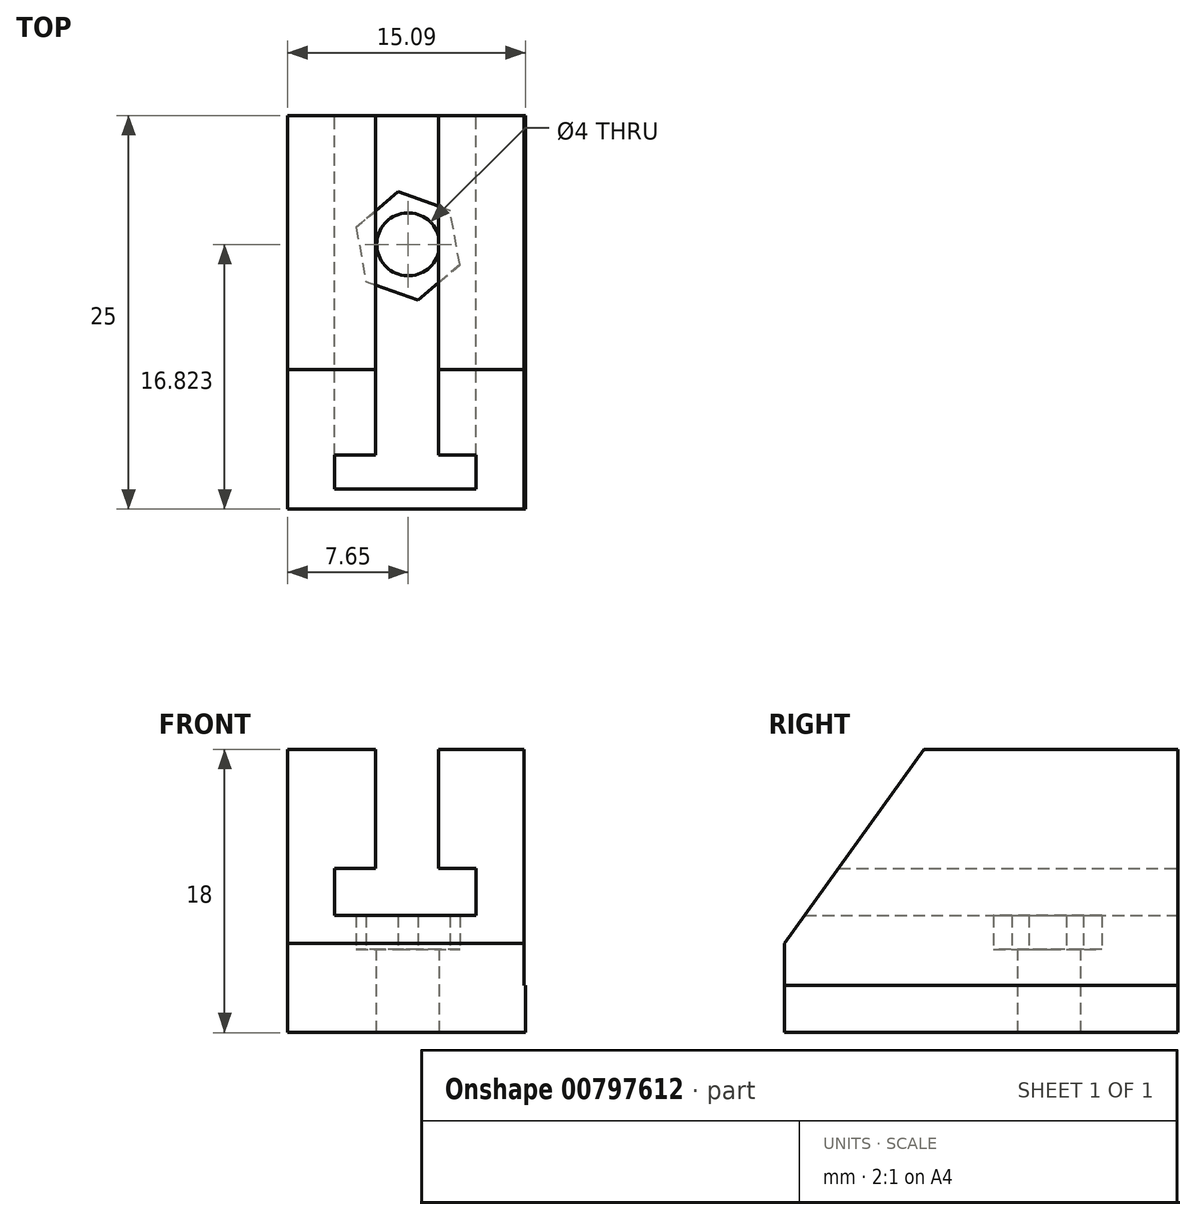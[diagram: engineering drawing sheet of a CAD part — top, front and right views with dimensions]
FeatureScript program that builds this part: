
annotation { "Feature Type Name" : "Feature", "Feature Type Description" : "" }
export const myFeature = defineFeature(function(context is Context, id is Id, definition is map)
    precondition{}
    {
        {
            var Q0;
            Q0=qCreatedBy(makeId("Front.planeOp"),FACE);
            var sketch = newSketch(context, id + "F0", { "sketchPlane" : qUnion([Q0])});
            skLineSegment(sketch, "E0.bottom", {"start": v(-7.65, 12.72) * mm, "end": v(-2.07, 12.72) * mm});
            skLineSegment(sketch, "E0.top", {"start": v(-7.65, -2.28) * mm, "end": v(7.35, -2.28) * mm});
            skLineSegment(sketch, "E0.left", {"start": v(-7.65, 12.72) * mm, "end": v(-7.65, -2.28) * mm});
            skLineSegment(sketch, "E0.right", {"start": v(7.35, 12.72) * mm, "end": v(7.35, -2.28) * mm});
            skLineSegment(sketch, "E1.bottom", {"start": v(-4.69, 5.16) * mm, "end": v(-2.07, 5.16) * mm});
            skLineSegment(sketch, "E1.top", {"start": v(-4.69, 2.16) * mm, "end": v(4.31, 2.16) * mm});
            skLineSegment(sketch, "E1.left", {"start": v(-4.69, 5.16) * mm, "end": v(-4.69, 2.16) * mm});
            skLineSegment(sketch, "E1.right", {"start": v(4.31, 5.16) * mm, "end": v(4.31, 2.16) * mm});
            skLineSegment(sketch, "E2.left", {"start": v(-2.07, 5.16) * mm, "end": v(-2.07, 12.72) * mm});
            skLineSegment(sketch, "E2.right", {"start": v(1.93, 5.16) * mm, "end": v(1.93, 12.72) * mm});
            skLineSegment(sketch, "E3.trimOffspring", {"start": v(1.93, 5.16) * mm, "end": v(4.31, 5.16) * mm});
            skLineSegment(sketch, "E4.bottom", {"start": v(-7.65, -2.28) * mm, "end": v(7.44, -2.28) * mm});
            skLineSegment(sketch, "E4.top", {"start": v(-7.65, -5.28) * mm, "end": v(7.44, -5.28) * mm});
            skLineSegment(sketch, "E4.left", {"start": v(-7.65, -2.28) * mm, "end": v(-7.65, -5.28) * mm});
            skLineSegment(sketch, "E4.right", {"start": v(7.44, -2.28) * mm, "end": v(7.44, -5.28) * mm});
            skLineSegment(sketch, "E5.trimOffspring", {"start": v(1.93, 12.72) * mm, "end": v(7.35, 12.72) * mm});
            skSolve(sketch);
        }
        {
            var Q0;
            Q0=makeQuery(id+"F0.imprint","IMPRINT",FACE,{"disambiguationData":[TD([[makeQuery(id+"F0.imprint","IMPRINT",EDGE,{"derivedFrom":sQuery(id+"F0.wireOp",EDGE,"E0.bottom")}),-1.0]])]});
            var Q1;
            Q1=makeQuery(id+"F0.imprint","IMPRINT",FACE,{"disambiguationData":[TD([[makeQuery(id+"F0.imprint","IMPRINT",EDGE,{"derivedFrom":sQuery(id+"F0.wireOp",EDGE,"E4.top")}),1.0]])]});
            extrude(context, id + "F1", {"entities" : qUnion([Q0, Q1]), "depth" : 25 * mm, "offsetDistance" : 25 * mm});
        }
        {
            var Q0;
            Q0=qCreatedBy(makeId("Right.planeOp"),FACE);
            var sketch = newSketch(context, id + "F2", { "sketchPlane" : qUnion([Q0])});
            skLineSegment(sketch, "E6", {"start": v(-27.17, -2.65) * mm, "end": v(-14.12, 15.54) * mm});
            skLineSegment(sketch, "E7", {"start": v(-14.12, 15.54) * mm, "end": v(-30.08, 15.54) * mm});
            skLineSegment(sketch, "E8", {"start": v(-30.08, 15.54) * mm, "end": v(-27.17, -2.65) * mm});
            skSolve(sketch);
        }
        {
            var Q0;
            Q0=makeQuery(id+"F2.imprint","IMPRINT",FACE,{"disambiguationData":[TD([[makeQuery(id+"F2.imprint","IMPRINT",EDGE,{"derivedFrom":sQuery(id+"F2.wireOp",EDGE,"E6")}),1.0]])]});
            extrude(context, id + "F3", {"entities" : qUnion([Q0]), "operationType" : NewBodyOperationType.REMOVE, "endBound" : BoundingType.SYMMETRIC, "oppositeDirection" : true, "depth" : 37.4 * mm, "offsetDistance" : 25 * mm});
        }
        {
            var Q0;
            Q0=qCreatedBy(makeId("Top.planeOp"),FACE);
            var sketch = newSketch(context, id + "F4", { "sketchPlane" : qUnion([Q0])});
            skPoint(sketch, "E9.0.midPoint", {"position": v(2.48, -5.83) * mm});
            skLineSegment(sketch, "E10.0", {"start": v(2.65, -6.02) * mm, "end": v(3.28, -9.46) * mm});
            skLineSegment(sketch, "E10.1", {"start": v(3.28, -9.46) * mm, "end": v(0.6, -11.73) * mm});
            skLineSegment(sketch, "E10.2", {"start": v(0.6, -11.73) * mm, "end": v(-2.69, -10.55) * mm});
            skLineSegment(sketch, "E10.3", {"start": v(-2.69, -10.55) * mm, "end": v(-3.31, -7.1) * mm});
            skLineSegment(sketch, "E10.4", {"start": v(-3.31, -7.1) * mm, "end": v(-0.64, -4.84) * mm});
            skLineSegment(sketch, "E10.5", {"start": v(-0.64, -4.84) * mm, "end": v(2.65, -6.02) * mm});
            skPoint(sketch, "E11.orphan", {"position": v(-3.1, -11.31) * mm});
            skPoint(sketch, "E12.orphan", {"position": v(4.26, -7.65) * mm});
            skPoint(sketch, "E13.orphan", {"position": v(0.7, -4.02) * mm});
            skArc(sketch, "E14.trimOffspring", {"start": v(2.65, -6.02) * mm, "mid": v(2.57, -5.93) * mm, "end": v(2.48, -5.83) * mm, "construction": true});
            skSolve(sketch);
        }
        {
            var Q0;
            Q0=qSketchRegion(id+"F4",true);
            extrude(context, id + "F5", {"entities" : qUnion([Q0]), "operationType" : NewBodyOperationType.REMOVE, "depth" : 3 * mm, "offsetDistance" : 25 * mm});
        }
        {
            var Q0;
            Q0=makeQuery(id+"F5.boolean.opBoolean","COPY",FACE,{"derivedFrom":makeQuery(id+"F5.opExtrude","CAP_FACE",FACE,{"disambiguationData":[OSD([sQuery(id+"F4.wireOp",EDGE,"E10.0"),sQuery(id+"F4.wireOp",EDGE,"E10.1"),sQuery(id+"F4.wireOp",EDGE,"E10.2"),sQuery(id+"F4.wireOp",EDGE,"E10.3"),sQuery(id+"F4.wireOp",EDGE,"E10.4"),sQuery(id+"F4.wireOp",EDGE,"E10.5")])],"isStart":true})});
            var sketch = newSketch(context, id + "F6", { "sketchPlane" : qUnion([Q0])});
            skCircle(sketch, "E15", {"center": v(0, -8.18) * mm, "radius": 2 * mm});
            skSolve(sketch);
        }
        {
            var Q0;
            Q0=qSketchRegion(id+"F6",true);
            extrude(context, id + "F7", {"entities" : qUnion([Q0]), "operationType" : NewBodyOperationType.REMOVE, "oppositeDirection" : true, "depth" : 25 * mm, "offsetDistance" : 25 * mm});
        }
    });
